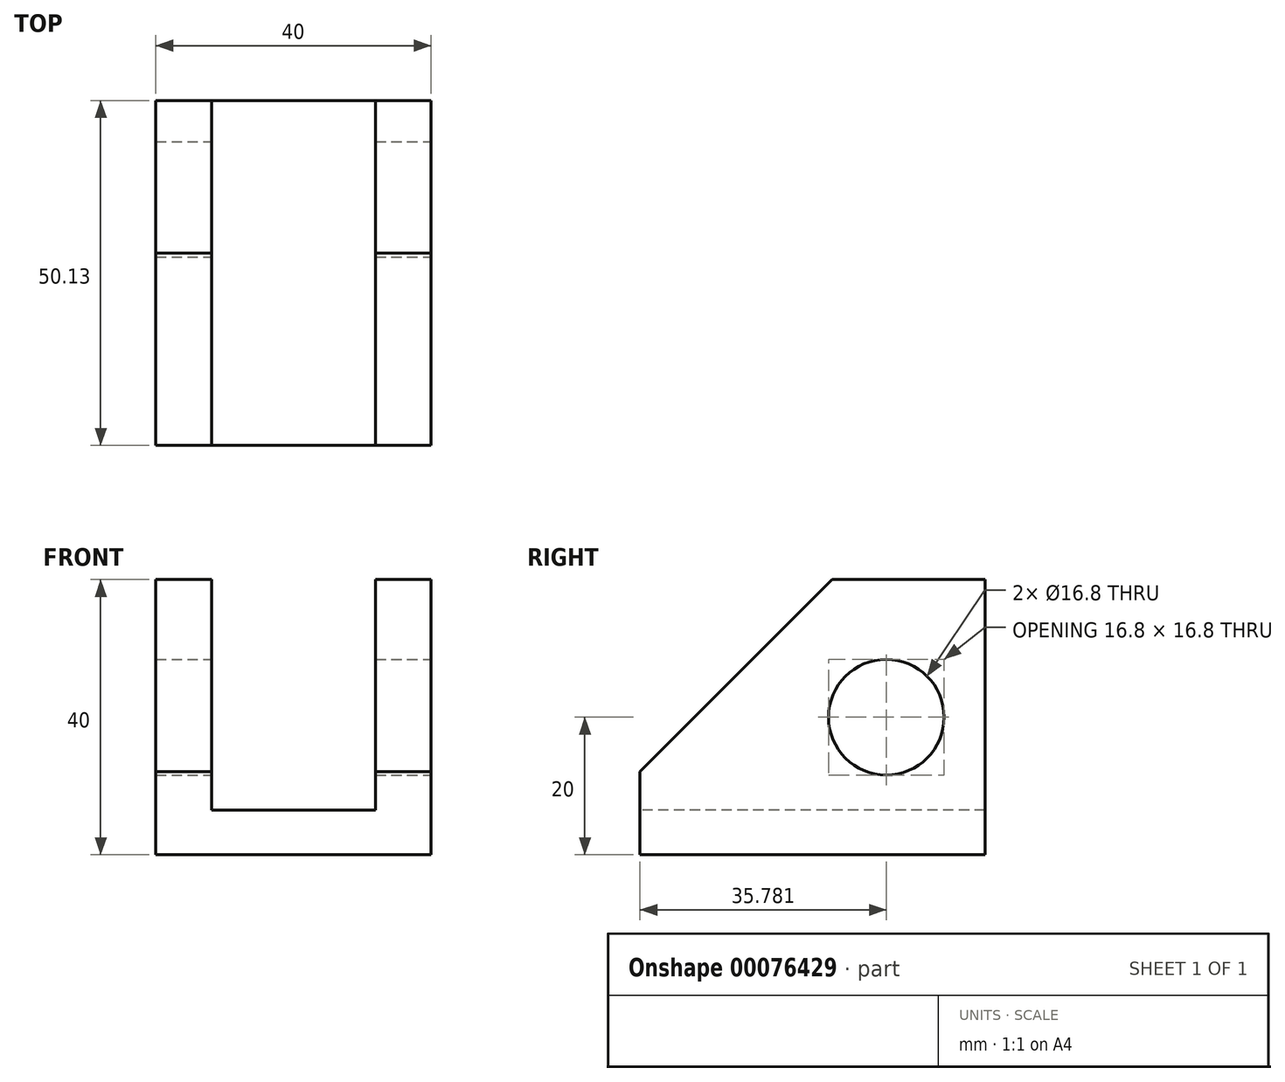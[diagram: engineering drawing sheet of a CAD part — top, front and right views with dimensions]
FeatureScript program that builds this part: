
annotation { "Feature Type Name" : "Feature", "Feature Type Description" : "" }
export const myFeature = defineFeature(function(context is Context, id is Id, definition is map)
    precondition{}
    {
        {
            var Q0;
            Q0=qCreatedBy(makeId("Front.planeOp"),FACE);
            var sketch = newSketch(context, id + "F0", { "sketchPlane" : qUnion([Q0])});
            skLineSegment(sketch, "E0.bottom", {"start": v(20, -20) * mm, "end": v(-20, -20) * mm});
            skLineSegment(sketch, "E0.top", {"start": v(20, 20) * mm, "end": v(-20, 20) * mm});
            skLineSegment(sketch, "E0.left", {"start": v(20, -20) * mm, "end": v(20, 20) * mm});
            skLineSegment(sketch, "E0.right", {"start": v(-20, -20) * mm, "end": v(-20, 20) * mm});
            skPoint(sketch, "E0.middle", {"position": v(0, 0) * mm});
            skSolve(sketch);
        }
        {
            var Q0;
            Q0 = qSketchRegion(id + "F0", true);
            extrude(context, id + "F1", {"entities" : qUnion([Q0]), "depth" : 42.38 * mm, "hasSecondDirection" : true, "secondDirectionOppositeDirection" : true, "secondDirectionDepth" : 7.75 * mm});
        }
        {
            var Q0;
            Q0=makeQuery(id+"F1.opExtrude","CAP_FACE",FACE,{"disambiguationData":[OSD([sQuery(id+"F0.wireOp",EDGE,"E0.bottom"),sQuery(id+"F0.wireOp",EDGE,"E0.top"),sQuery(id+"F0.wireOp",EDGE,"E0.left"),sQuery(id+"F0.wireOp",EDGE,"E0.right")])],"isStart":false});
            var sketch = newSketch(context, id + "F2", { "sketchPlane" : qUnion([Q0])});
            skLineSegment(sketch, "E1.bottom", {"start": v(-11.91, 20) * mm, "end": v(0, 20) * mm});
            skLineSegment(sketch, "E1.top", {"start": v(-11.91, -13.47) * mm, "end": v(0, -13.47) * mm});
            skLineSegment(sketch, "E1.left", {"start": v(-11.91, 20) * mm, "end": v(-11.91, -13.47) * mm});
            skLineSegment(sketch, "E1.right", {"start": v(0, 20) * mm, "end": v(0, -13.47) * mm});
            skLineSegment(sketch, "E2.MirrorCS", {"start": v(11.91, 20) * mm, "end": v(0, 20) * mm});
            skLineSegment(sketch, "E3.MirrorCS", {"start": v(11.91, 20) * mm, "end": v(11.91, -13.47) * mm});
            skLineSegment(sketch, "E4.MirrorCS", {"start": v(11.91, -13.47) * mm, "end": v(0, -13.47) * mm});
            skSolve(sketch);
        }
        {
            var Q0;
            Q0 = qSketchRegion(id + "F2", true);
            extrude(context, id + "F3", {"entities" : qUnion([Q0]), "operationType" : NewBodyOperationType.REMOVE, "oppositeDirection" : true, "depth" : 52.48 * mm});
        }
        {
            var Q0;
            {var subQ0=sQuery(id+"F0.wireOp",EDGE,"E0.right");var subQ1=sQuery(id+"F0.wireOp",EDGE,"E0.top");Q0=makeQuery(id+"F3.boolean.opBoolean","SPLIT",EDGE,{"disambiguationData":[TD([makeQuery(id+"F1.opExtrude","SWEPT_FACE",FACE,{"disambiguationData":[OSD([subQ0])]})])],"derivedFrom":makeQuery(id+"F1.opExtrude","CAP_EDGE",EDGE,{"disambiguationData":[OSD([subQ1])],"isStart":false})});}
            var Q1;
            {var subQ0=sQuery(id+"F0.wireOp",EDGE,"E0.left");var subQ1=sQuery(id+"F0.wireOp",EDGE,"E0.top");Q1=makeQuery(id+"F3.boolean.opBoolean","SPLIT",EDGE,{"disambiguationData":[TD([makeQuery(id+"F1.opExtrude","SWEPT_FACE",FACE,{"disambiguationData":[OSD([subQ0])]})])],"derivedFrom":makeQuery(id+"F1.opExtrude","CAP_EDGE",EDGE,{"disambiguationData":[OSD([subQ1])],"isStart":false})});}
            chamfer(context, id + "F4", {"entities" : qUnion([Q0, Q1]), "width" : 27.94 * mm, "tangentPropagation" : true});
        }
        {
            var Q0;
            Q0=makeQuery(id+"F1.opExtrude","SWEPT_FACE",FACE,{"disambiguationData":[OSD([sQuery(id+"F0.wireOp",EDGE,"E0.left")])]});
            var sketch = newSketch(context, id + "F5", { "sketchPlane" : qUnion([Q0])});
            skCircle(sketch, "E5", {"center": v(-6.6, 0) * mm, "radius": 8.4 * mm});
            skSolve(sketch);
        }
        {
            var Q0;
            Q0 = qSketchRegion(id + "F5", true);
            extrude(context, id + "F6", {"entities" : qUnion([Q0]), "operationType" : NewBodyOperationType.REMOVE, "oppositeDirection" : true, "depth" : 40 * mm});
        }
    });
